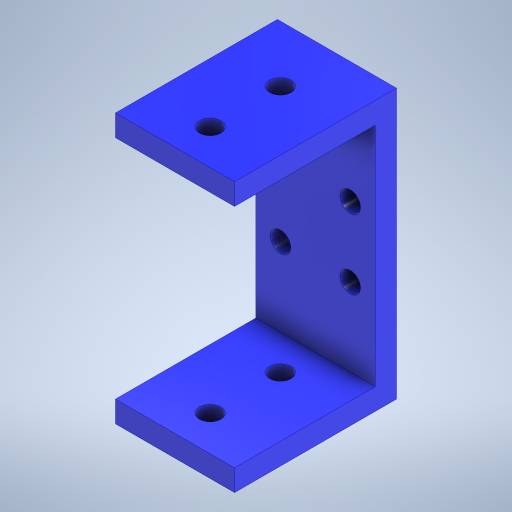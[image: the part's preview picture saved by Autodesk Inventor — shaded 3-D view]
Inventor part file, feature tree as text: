
AUTODESK INVENTOR PART (.ipt)
format: ipt  version: 2023 (Build 270158000, 158)  size: 296,960 bytes
history: native  units: mm
features: extrude x3, sketch x3
ambient origin geometry x8: Origin, YZ Plane, XZ Plane, XY Plane, X Axis, Y Axis, Z Axis, Center Point
bodies: Solid1 (feature_tree)
feature tree (6):
  extrude  "Extrusion1"  Depth=10.0mm TaperAngle=0.0deg
  extrude  "Extrusion2"  Depth=10.0mm
  extrude  "Extrusion3"  Depth=10.0mm
  sketch  "Sketch1"  dims[d2=125.5mm d3=10.0mm d4=0.0mm]
  sketch  "Sketch2"  dims[d5=10.0mm d6=10.0mm]
  sketch  "Sketch3"  dims[d7=65.5mm d8=0.0mm d9=10.0mm d10=10.0mm d11=0.0mm d12=0.0mm]
